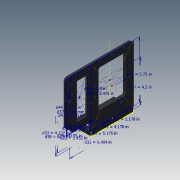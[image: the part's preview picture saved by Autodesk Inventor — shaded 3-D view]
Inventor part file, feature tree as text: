
AUTODESK INVENTOR PART (.ipt)
format: ipt  version: 2020.3 (Build 243373000, 373)  size: 279,040 bytes
history: native  units: in
note: dims shown in document units (in); Inventor stores cm internally (conversion verified against a paired STEP export)
features: sketch x9, fillet x7, extrude x6, hole x3, chamfer x1, projected_geometry x1
ambient origin geometry x8: Origin, YZ Plane, XZ Plane, XY Plane, X Axis, Y Axis, Z Axis, Center Point
bodies: Solid1 (feature_tree)
feature tree (27):
  extrude  "Extrusion1"  Depth=1.07in
  sketch  "Sketch2"  dims[d3=4.25in d4=0.5in]
  sketch  "Sketch4"  dims[d8=0.5in d9=0.0in d10=5.75in]
  extrude  "Extrusion3"  Depth=0.5in
  sketch  "Sketch3"  dims[d6=0.375in d7=0.0in]
  extrude  "Extrusion2"  TaperAngle=0.0deg  [1 undecoded]
  hole  "Hole1"  [1 undecoded]
  sketch  "Sketch6"  dims[d15=1.325in d16=0.375in d17=0.0in d18=1.3in d19=2.5in]
  extrude  "Extrusion4"  Depth=0.13in
  fillet  "Fillet3"  Radius=3.8in
  hole  "Hole2"  [1 undecoded]
  fillet  "Fillet1"  Radius=1.3in
  fillet  "Fillet2"  Radius=2.5in
  hole  "Hole3"  [1 undecoded]
  fillet  "Fillet4"  Radius=1.452in
  fillet  "Fillet5"  Radius=1.178in
  extrude  "Extrusion5"  Depth=0.1875in
  fillet  "Fillet6"  Radius=4.137in
  extrude  "Extrusion6"  Depth=0.125in
  chamfer  "Chamfer1"  Distance=0.5in
  fillet  "Fillet7"  Radius=1.5748in
  sketch  "Sketch1"  dims[d0=3.2in d1=1.07in]
  sketch  "Sketch5"  dims[d11=0.23in d12=0.0in d13=0.13in d14=3.8in]
  sketch  "Sketch7"  dims[d20=0.55in d21=0.45in d22=1.452in d23=1.178in]
  sketch  "Sketch8"  dims[d24=4.178in]
  sketch  "Sketch9"  dims[d25=0.25in d26=0.75in d27=0.315in d28=0.157in d29=0.5635in d30=1.0in d31=0.8108in d32=6.404in d33=4.137in d34=0.125in d35=0.5in d36=1.5748in d37=4.1732in d38=3.75in d39=5.175in d40=0.1in d41=0.0in d42=0.05in d43=0.2in d44=1.75in d45=3.475in d46=0.9in d47=4.2in d48=0.104in d49=0.276in d50=0.315in d51=0.157in d52=0.5635in d53=0.432in d54=0.8108in d55=0.15in d56=0.093in d57=0.276in d58=0.315in d59=0.157in d60=0.5635in d61=0.432in d62=0.8108in d63=0.25in d64=0.1875in d65=2.75in d66=3.725in d67=1.715in d68=0.0in d69=0.1875in d70=1.815in d71=0.0in d72=0.125in d73=0.125in d74=45.0deg d75=0.5in d76=0.5in d77=0.1875in]
  projected_geometry  "Projected Loop1"
note: 4 required parameter values undecoded (feature->parameter linkage not recoverable at this tier; creation-order binding heuristic only, values carry confidence <= 0.55)
